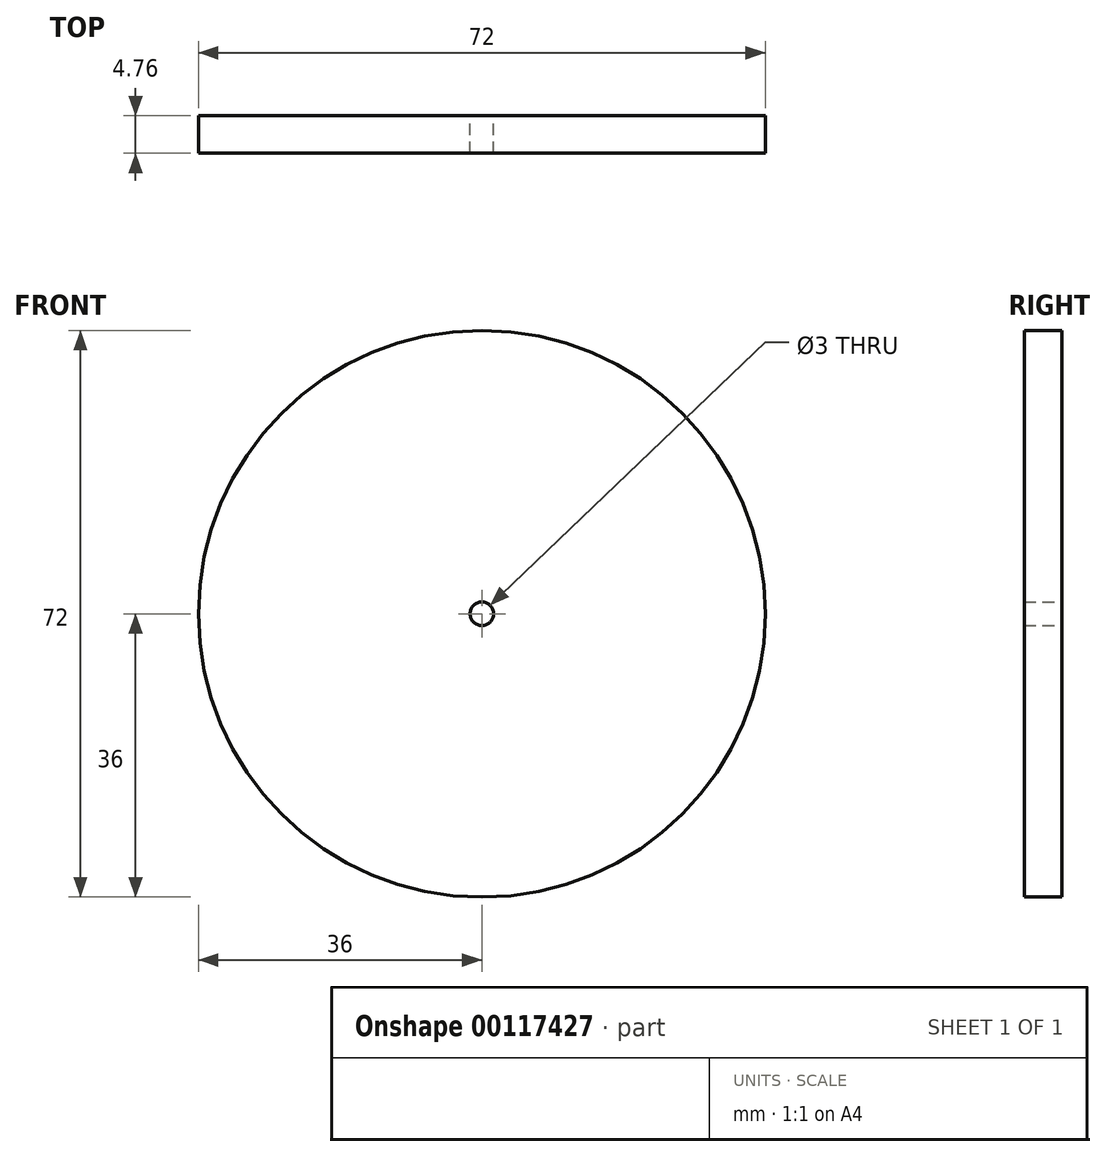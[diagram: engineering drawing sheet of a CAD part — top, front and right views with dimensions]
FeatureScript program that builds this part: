
annotation { "Feature Type Name" : "Feature", "Feature Type Description" : "" }
export const myFeature = defineFeature(function(context is Context, id is Id, definition is map)
    precondition{}
    {
        {
            var Q0;
            Q0=qCreatedBy(makeId("Front.planeOp"),FACE);
            var sketch = newSketch(context, id + "F0", { "sketchPlane" : qUnion([Q0])});
            skCircle(sketch, "E0", {"center": v(0, 0) * mm, "radius": 36 * mm});
            skCircle(sketch, "E1", {"center": v(0, 0) * mm, "radius": 1.5 * mm});
            skSolve(sketch);
        }
        {
            var Q0;
            Q0=makeQuery(id+"F0.imprint","IMPRINT",FACE,{"disambiguationData":[TD([[makeQuery(id+"F0.imprint","IMPRINT",EDGE,{"derivedFrom":sQuery(id+"F0.wireOp",EDGE,"E0")}),1.0]])]});
            var Q1;
            Q1=sQuery(id+"F0.wireOp",EDGE,"E1");
            var Q2;
            Q2=sQuery(id+"F0.wireOp",EDGE,"E0");
            extrude(context, id + "F1", {"entities" : qUnion([Q0]), "surfaceEntities" : qUnion([Q1, Q2]), "depth" : 4.76 * mm});
        }
    });
